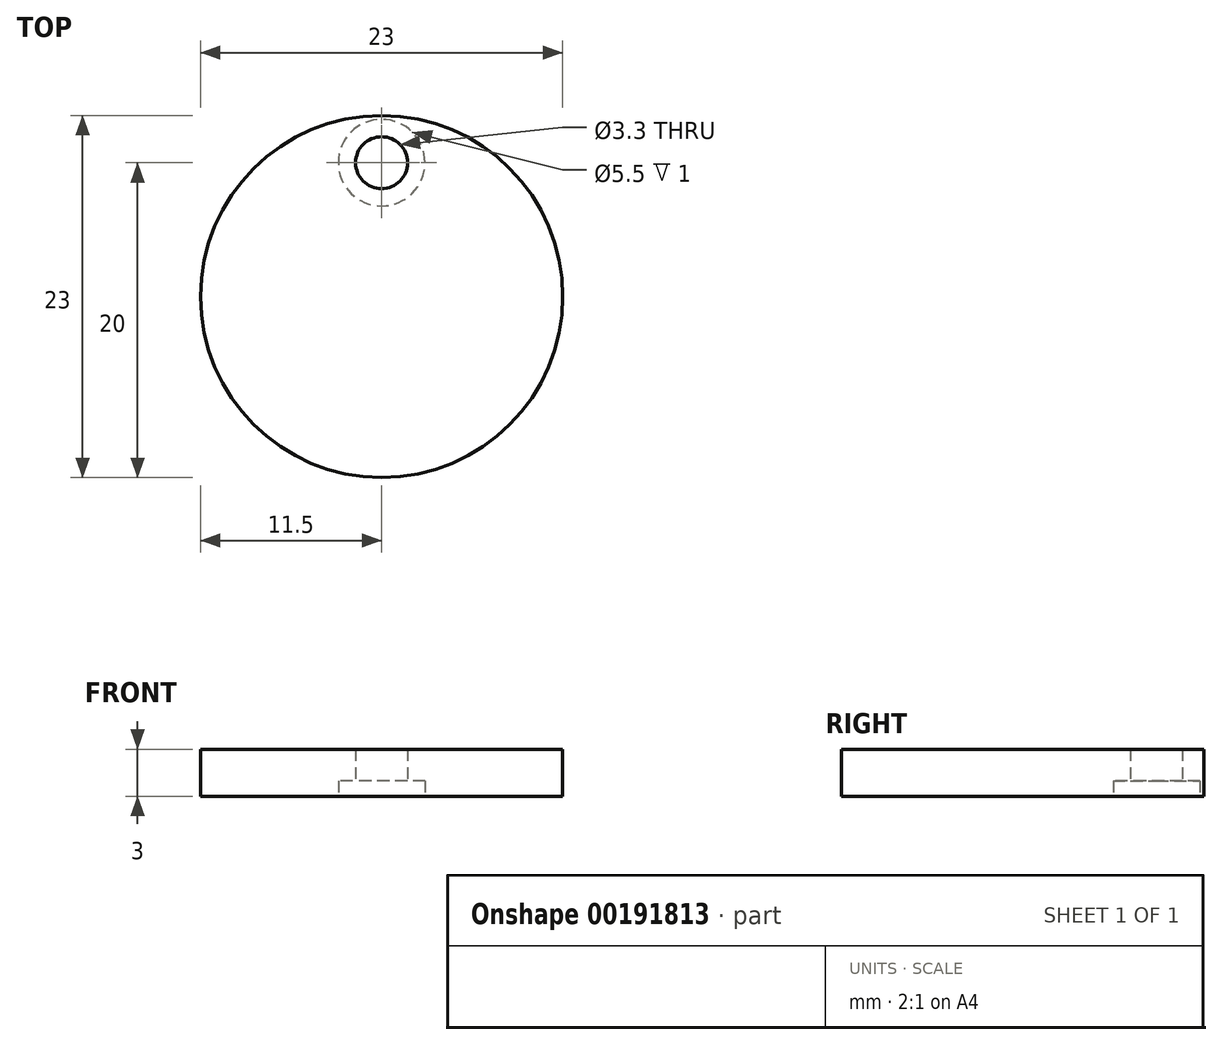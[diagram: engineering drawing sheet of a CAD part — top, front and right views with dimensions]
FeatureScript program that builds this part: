
annotation { "Feature Type Name" : "Feature", "Feature Type Description" : "" }
export const myFeature = defineFeature(function(context is Context, id is Id, definition is map)
    precondition{}
    {
        {
            var Q0;
            Q0=qCreatedBy(makeId("Top.planeOp"),FACE);
            var sketch = newSketch(context, id + "F0", { "sketchPlane" : qUnion([Q0])});
            skCircle(sketch, "E0", {"center": v(0, 0) * mm, "radius": 11.5 * mm});
            skCircle(sketch, "E1", {"center": v(0, 8.5) * mm, "radius": 1.65 * mm});
            skCircle(sketch, "E2", {"center": v(0, 8.5) * mm, "radius": 2.75 * mm});
            skSolve(sketch);
        }
        {
            var Q0;
            Q0=makeQuery(id+"F0.imprint","IMPRINT",FACE,{"disambiguationData":[TD([[makeQuery(id+"F0.imprint","IMPRINT",EDGE,{"derivedFrom":sQuery(id+"F0.wireOp",EDGE,"E0")}),1.0]])]});
            var Q1;
            Q1=makeQuery(id+"F0.imprint","IMPRINT",FACE,{"disambiguationData":[TD([[makeQuery(id+"F0.imprint","IMPRINT",EDGE,{"derivedFrom":sQuery(id+"F0.wireOp",EDGE,"E1")}),-1.0]])]});
            extrude(context, id + "F1", {"entities" : qUnion([Q0, Q1]), "depth" : 3 * mm});
        }
        {
            var Q0;
            Q0=makeQuery(id+"F0.imprint","IMPRINT",FACE,{"disambiguationData":[TD([[makeQuery(id+"F0.imprint","IMPRINT",EDGE,{"derivedFrom":sQuery(id+"F0.wireOp",EDGE,"E1")}),-1.0]])]});
            extrude(context, id + "F2", {"entities" : qUnion([Q0]), "operationType" : NewBodyOperationType.REMOVE, "depth" : 1 * mm});
        }
    });
